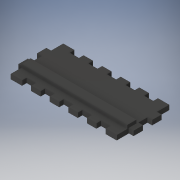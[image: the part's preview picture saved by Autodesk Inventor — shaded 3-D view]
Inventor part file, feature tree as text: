
AUTODESK INVENTOR PART (.ipt)
format: ipt  version: 2019 (Build 230136000, 136)  size: 208,896 bytes
history: native  units: mm
features: extrude x3, sketch x3
ambient origin geometry x8: Origin, YZ Plane, XZ Plane, XY Plane, X Axis, Y Axis, Z Axis, Center Point
bodies: Solid1 (feature_tree)
feature tree (6):
  extrude  "Extrusion1"  Depth=45.0mm
  extrude  "Extrusion2"  Depth=4.0mm
  extrude  "Extrusion3"  Depth=4.0mm
  sketch  "Sketch1"  dims[d0=99.0mm d1=45.0mm]
  sketch  "Sketch2"  dims[d6=4.0mm d7=0.0mm d8=4.0mm]
  sketch  "Sketch3"  dims[d11=8.0mm d12=4.0mm d14=8.0mm d15=8.0mm d16=8.0mm d17=4.0mm d18=8.0mm d19=4.0mm d20=0.0mm d21=8.0mm d22=5.0mm d23=3.0mm d24=0.0mm]
